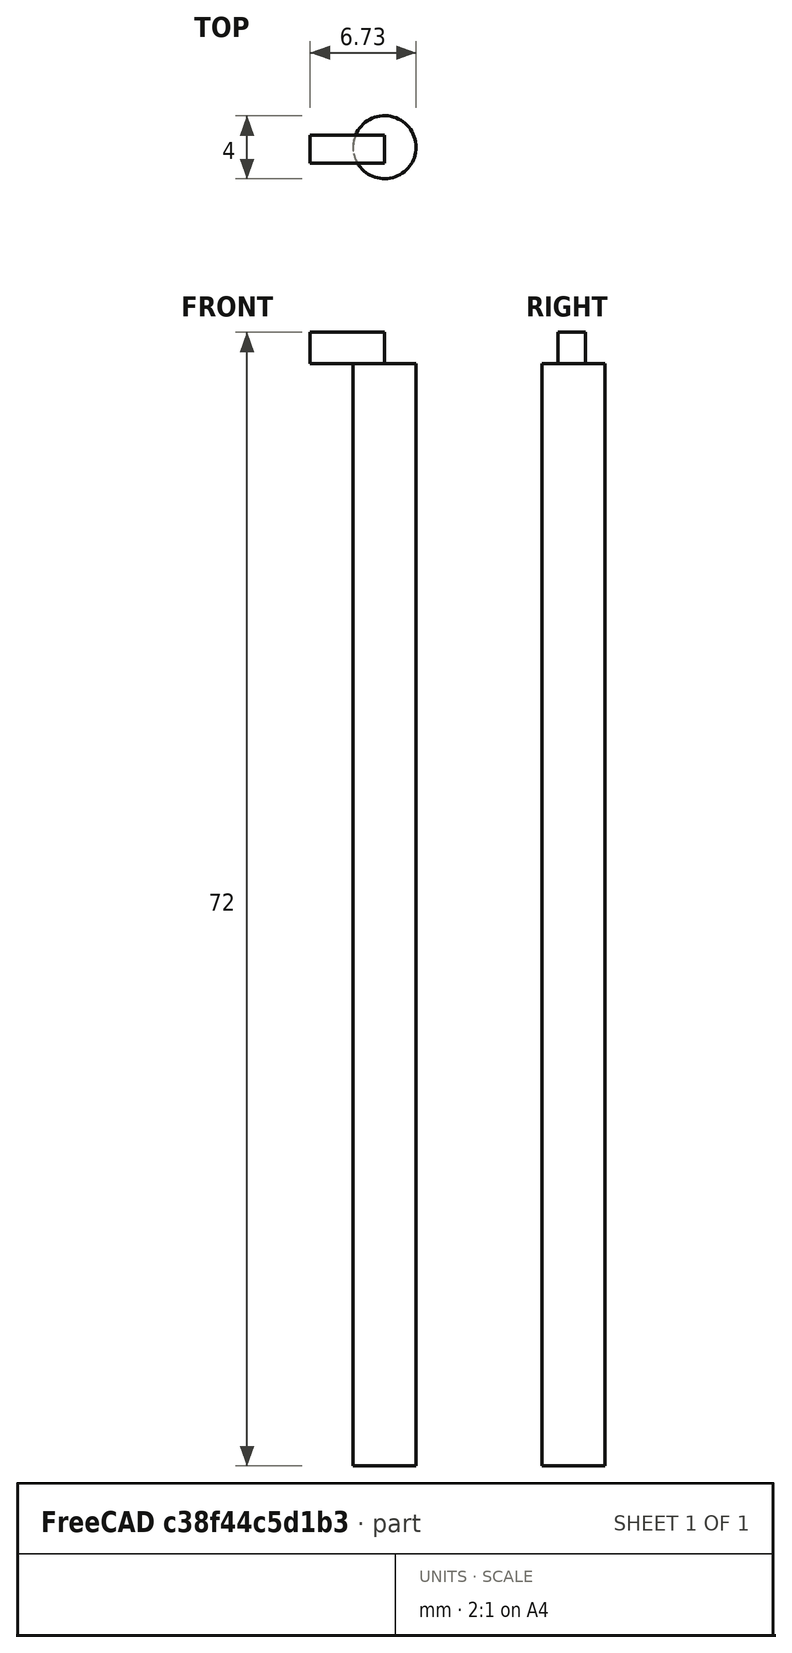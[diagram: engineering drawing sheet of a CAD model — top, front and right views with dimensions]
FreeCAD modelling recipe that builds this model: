
FCSTD DOCUMENT  (FreeCAD 0.16R6706 (Git))
Label: Cylindre
License: All rights reserved
LicenseURL: http://en.wikipedia.org/wiki/All_rights_reserved
objects: Sketcher::SketchObject×2, PartDesign::Pad×2
note: 6 computed .brp shape members not serialized (recipe doc carries the construction recipe); baked Part::Feature solids carry a one-line shape summary decoded from their .brp

FEATURE [Sketcher::SketchObject] Sketch
  Placement = pos=(0,0,0) rot=(1,0,0;3.14159rad)
  sketch-geometry (1):
    g0: Circle CenterX=0 CenterY=0 CenterZ=0 NormalX=0 NormalY=0 NormalZ=1 Radius=2
  constraints (2):
    c: Coincident(g0,g-1)
    c: Radius(g0) = 2
FEATURE [PartDesign::Pad] Pad
  Length = 70
  Length2 = 100
  Placement = pos=(0,0,0) rot=(1,0,0;3.14159rad)
  Sketch = -> Sketch
  Type = 0
FEATURE [Sketcher::SketchObject] Sketch001
  sketch-geometry (4):
    g0: LineSegment StartX=-4.72805 StartY=0.757583 StartZ=0 EndX=0 EndY=0.757583 EndZ=0
    g1: LineSegment StartX=0 StartY=0.757583 StartZ=0 EndX=0 EndY=-1 EndZ=0
    g2: LineSegment StartX=0 StartY=-1 StartZ=0 EndX=-4.72805 EndY=-1 EndZ=0
    g3: LineSegment StartX=-4.72805 StartY=-1 StartZ=0 EndX=-4.72805 EndY=0.757583 EndZ=0
  constraints (9):
    c: Coincident(g0,g1)
    c: Coincident(g1,g2)
    c: Coincident(g2,g3)
    c: Coincident(g3,g0)
    c: Horizontal(g0)
    c: Horizontal(g2)
    c: Vertical(g1)
    c: Vertical(g3)
    c: PointOnObject(g1,g-2)
FEATURE [PartDesign::Pad] Pad001
  Length = 2
  Length2 = 100
  Sketch = -> Sketch001
  Type = 0
